# Revit family: O19001001_Lavamanos San Lorenzo para Incrustar Blanco
name_source: partatom
category: Plumbing Fixtures
units: mm (PartAtom-declared; Revit-internal decimal feet)

## family parameters
Cut with Voids When Loaded = Yes
Host = Face
OmniClass Number = 23.31.13.11
OmniClass Title = Single Sinks
Part Type = Normal
Room Calculation Point = No
Round Connector Dimension = Use Diameter
Shared = No

## types (1)
- O19001001_Lavamanos San Lorenzo para Incrustar Blanco
    Ancho = 487 mm  [stored 1.59777 ft]
    Creado por = IDD
    Default Elevation = 1219 mm
    Description = Lavamanos de incrustar en Porcelana Sanitaria
    Dimensiones del producto empacado = 20 1/8 x 16 7/8 x 9 1/4 (51 cm x 43 cm x 23.5 cm)
    Fecha de creación = 13/08/2020
    Garantía = Garantía Integral de por vida
    Manufacturer = Corona
    Material = Corona_Porcelana_Sanitaria_Blanco
    Model = San Lorenzo
    Normatividad = Cumple con los requerimientos ADA para accesibilidad de personas discapacitadas - Icontec NTC 920 y ASME/ANSI A112.19.2
    Peso del producto empacado = 17.2 lbs (7.8 kg)
    Pozo = 16 3/4 x 14 (42.5 cm x 35.5 cm)
    Profundidad = 421 mm  [stored 1.38123 ft]
    Referencia = O19001001
    URL = https://corona.co

note: [stored X ft] marks values corroborated as IEEE doubles in the binary element streams (Revit-internal decimal feet)

## geometry (parser evidence)
native form markers: Sweep x7
no freeform markers — native parametric forms only
